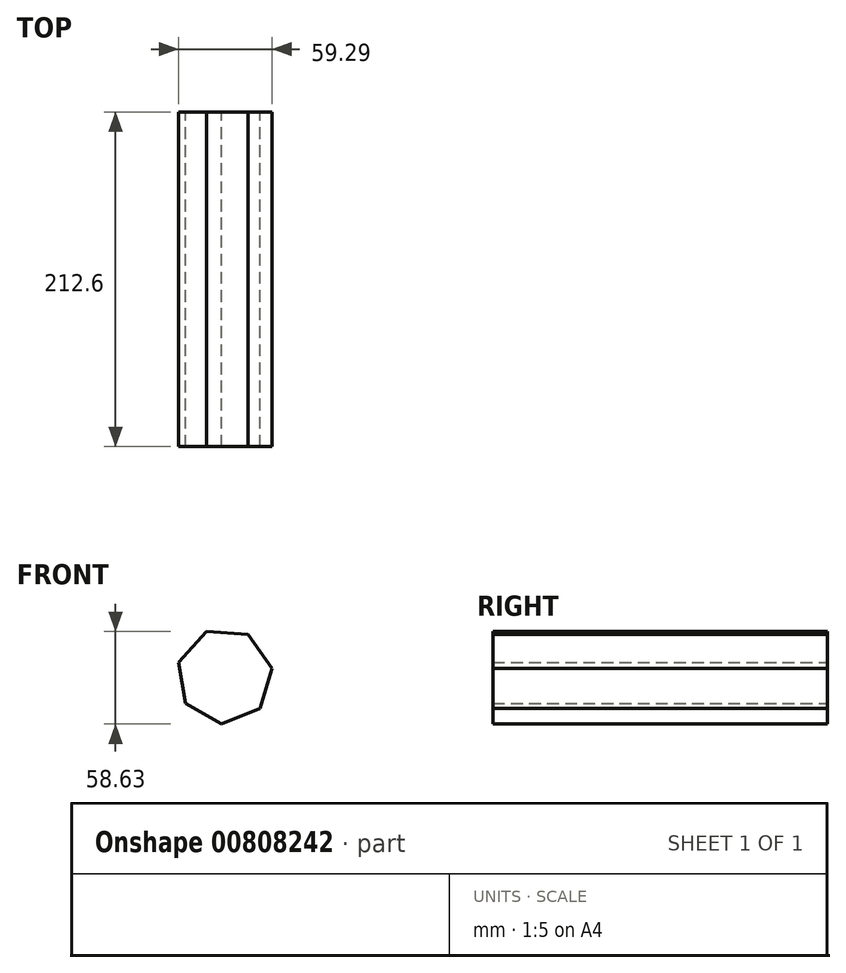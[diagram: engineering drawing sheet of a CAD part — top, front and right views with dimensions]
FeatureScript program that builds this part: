
annotation { "Feature Type Name" : "Feature", "Feature Type Description" : "" }
export const myFeature = defineFeature(function(context is Context, id is Id, definition is map)
    precondition{}
    {
        {
            var Q0;
            Q0=qCreatedBy(makeId("Front.planeOp"),FACE);
            var sketch = newSketch(context, id + "F0", { "sketchPlane" : qUnion([Q0])});
            skCircle(sketch, "E0.cCircle", {"center": v(0, 0) * mm, "radius": 27.45 * mm, "construction": true});
            skLineSegment(sketch, "E0.0", {"start": v(30.07, 4.91) * mm, "end": v(22.59, -20.45) * mm});
            skLineSegment(sketch, "E0.1", {"start": v(22.59, -20.45) * mm, "end": v(-1.9, -30.4) * mm});
            skLineSegment(sketch, "E0.2", {"start": v(-1.9, -30.4) * mm, "end": v(-24.96, -17.47) * mm});
            skLineSegment(sketch, "E0.3", {"start": v(-24.96, -17.47) * mm, "end": v(-29.22, 8.62) * mm});
            skLineSegment(sketch, "E0.4", {"start": v(-29.22, 8.62) * mm, "end": v(-11.48, 28.22) * mm});
            skLineSegment(sketch, "E0.5", {"start": v(-11.48, 28.22) * mm, "end": v(14.9, 26.57) * mm});
            skLineSegment(sketch, "E0.6", {"start": v(14.9, 26.57) * mm, "end": v(30.07, 4.91) * mm});
            skPoint(sketch, "E0.0.midPoint", {"position": v(26.33, -7.77) * mm});
            skSolve(sketch);
        }
        {
            var Q0;
            Q0 = qSketchRegion(id + "F0", true);
            extrude(context, id + "F1", {"entities" : qUnion([Q0]), "depth" : 212.6 * mm, "offsetDistance" : 25.4 * mm});
        }
        {
            var Q0;
            Q0=makeQuery(id+"F1.opExtrude","CAP_FACE",FACE,{"disambiguationData":[OSD([sQuery(id+"F0.wireOp",EDGE,"E0.0"),sQuery(id+"F0.wireOp",EDGE,"E0.1"),sQuery(id+"F0.wireOp",EDGE,"E0.2"),sQuery(id+"F0.wireOp",EDGE,"E0.3"),sQuery(id+"F0.wireOp",EDGE,"E0.4"),sQuery(id+"F0.wireOp",EDGE,"E0.5"),sQuery(id+"F0.wireOp",EDGE,"E0.6")])],"isStart":false});
            shell(context, id + "F2", {"entities" : qUnion([Q0]), "thickness" : 889 * mm});
        }
    });
